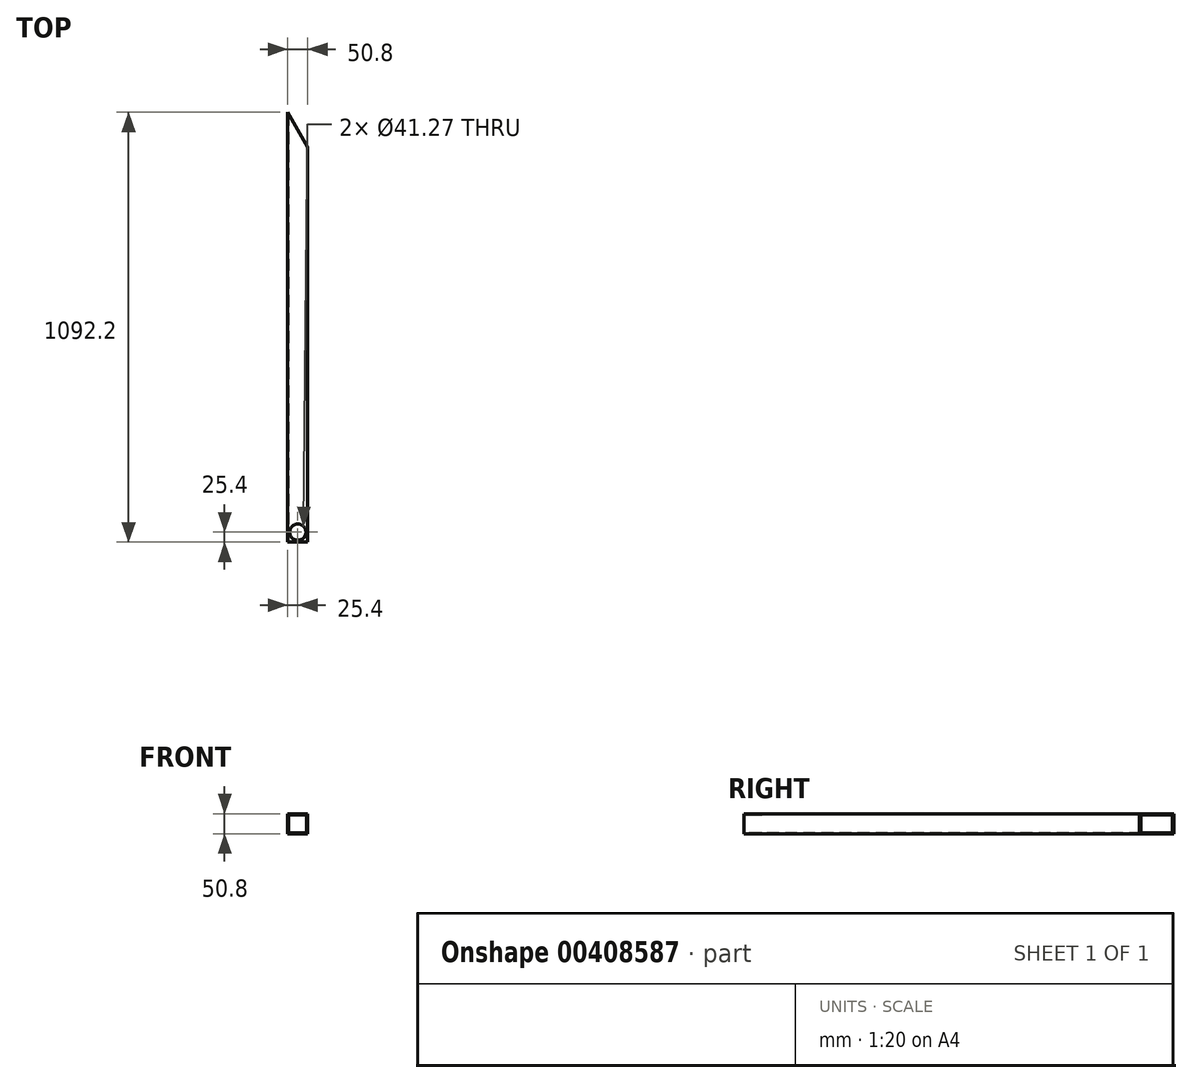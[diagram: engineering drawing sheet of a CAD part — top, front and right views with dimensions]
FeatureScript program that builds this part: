
annotation { "Feature Type Name" : "Feature", "Feature Type Description" : "" }
export const myFeature = defineFeature(function(context is Context, id is Id, definition is map)
    precondition{}
    {
        {
            var Q0;
            Q0=qCreatedBy(makeId("Front.planeOp"),FACE);
            var sketch = newSketch(context, id + "F0", { "sketchPlane" : qUnion([Q0])});
            skLineSegment(sketch, "E0.bottom", {"start": v(25.4, -25.4) * mm, "end": v(-25.4, -25.4) * mm});
            skLineSegment(sketch, "E0.top", {"start": v(25.4, 25.4) * mm, "end": v(-25.4, 25.4) * mm});
            skLineSegment(sketch, "E0.left", {"start": v(25.4, -25.4) * mm, "end": v(25.4, 25.4) * mm});
            skLineSegment(sketch, "E0.right", {"start": v(-25.4, -25.4) * mm, "end": v(-25.4, 25.4) * mm});
            skPoint(sketch, "E0.middle", {"position": v(0, 0) * mm});
            skSolve(sketch);
        }
        {
            var Q0;
            Q0=makeQuery(id+"F0.imprint","IMPRINT",FACE,{"disambiguationData":[TD([[makeQuery(id+"F0.imprint","IMPRINT",EDGE,{"derivedFrom":sQuery(id+"F0.wireOp",EDGE,"E0.bottom")}),-1.0]])]});
            extrude(context, id + "F1", {"entities" : qUnion([Q0]), "endBound" : BoundingType.SYMMETRIC, "oppositeDirection" : true, "depth" : 1092.2 * mm});
        }
        {
            var Q0;
            Q0=makeQuery(id+"F1.opExtrude","CAP_FACE",FACE,{"disambiguationData":[OSD([sQuery(id+"F0.wireOp",EDGE,"E0.bottom"),sQuery(id+"F0.wireOp",EDGE,"E0.top"),sQuery(id+"F0.wireOp",EDGE,"E0.left"),sQuery(id+"F0.wireOp",EDGE,"E0.right")])],"isStart":true});
            var Q1;
            Q1=makeQuery(id+"F1.opExtrude","CAP_FACE",FACE,{"disambiguationData":[OSD([sQuery(id+"F0.wireOp",EDGE,"E0.bottom"),sQuery(id+"F0.wireOp",EDGE,"E0.top"),sQuery(id+"F0.wireOp",EDGE,"E0.left"),sQuery(id+"F0.wireOp",EDGE,"E0.right")])],"isStart":false});
            shell(context, id + "F2", {"entities" : qUnion([Q0, Q1]), "thickness" : 2.54 * mm});
        }
        {
            var Q0;
            Q0=makeQuery(id+"F1.opExtrude","CAP_EDGE",EDGE,{"disambiguationData":[OSD([sQuery(id+"F0.wireOp",EDGE,"E0.left")])],"isStart":false});
            chamfer(context, id + "F3", {"entities" : qUnion([Q0]), "chamferType" : ChamferType.OFFSET_ANGLE, "width" : 50.8 * mm, "oppositeDirection" : true, "angle" : 60 * degree, "tangentPropagation" : true});
        }
        {
            var Q0;
            Q0=makeQuery(id+"F1.opExtrude","SWEPT_FACE",FACE,{"disambiguationData":[OSD([sQuery(id+"F0.wireOp",EDGE,"E0.top")])]});
            var sketch = newSketch(context, id + "F4", { "sketchPlane" : qUnion([Q0])});
            skPoint(sketch, "E1", {"position": v(0, -520.7) * mm});
            skPoint(sketch, "E1.positionSnap0", {"position": v(0, -546.1) * mm});
            skSolve(sketch);
        }
        {
            var Q0;
            Q0=sQuery(id+"F4.wireOp",VERTEX,"E1");
            var Q1;
            Q1=makeQuery(id+"F1.opExtrude","SWEPT_BODY",BODY,{"disambiguationData":[OSD([sQuery(id+"F0.wireOp",EDGE,"E0.bottom"),sQuery(id+"F0.wireOp",EDGE,"E0.top"),sQuery(id+"F0.wireOp",EDGE,"E0.left"),sQuery(id+"F0.wireOp",EDGE,"E0.right")])]});
            hole(context, id + "F5", {"style" : HoleStyle.SIMPLE, "endStyle" : HoleEndStyle.THROUGH, "holeDiameter" : 41.27 * mm, "isTappedThrough" : true, "tappedDepth" : 12.7 * mm, "tapClearance" : 3, "locations" : qUnion([Q0]), "scope" : qUnion([Q1])});
        }
    });
